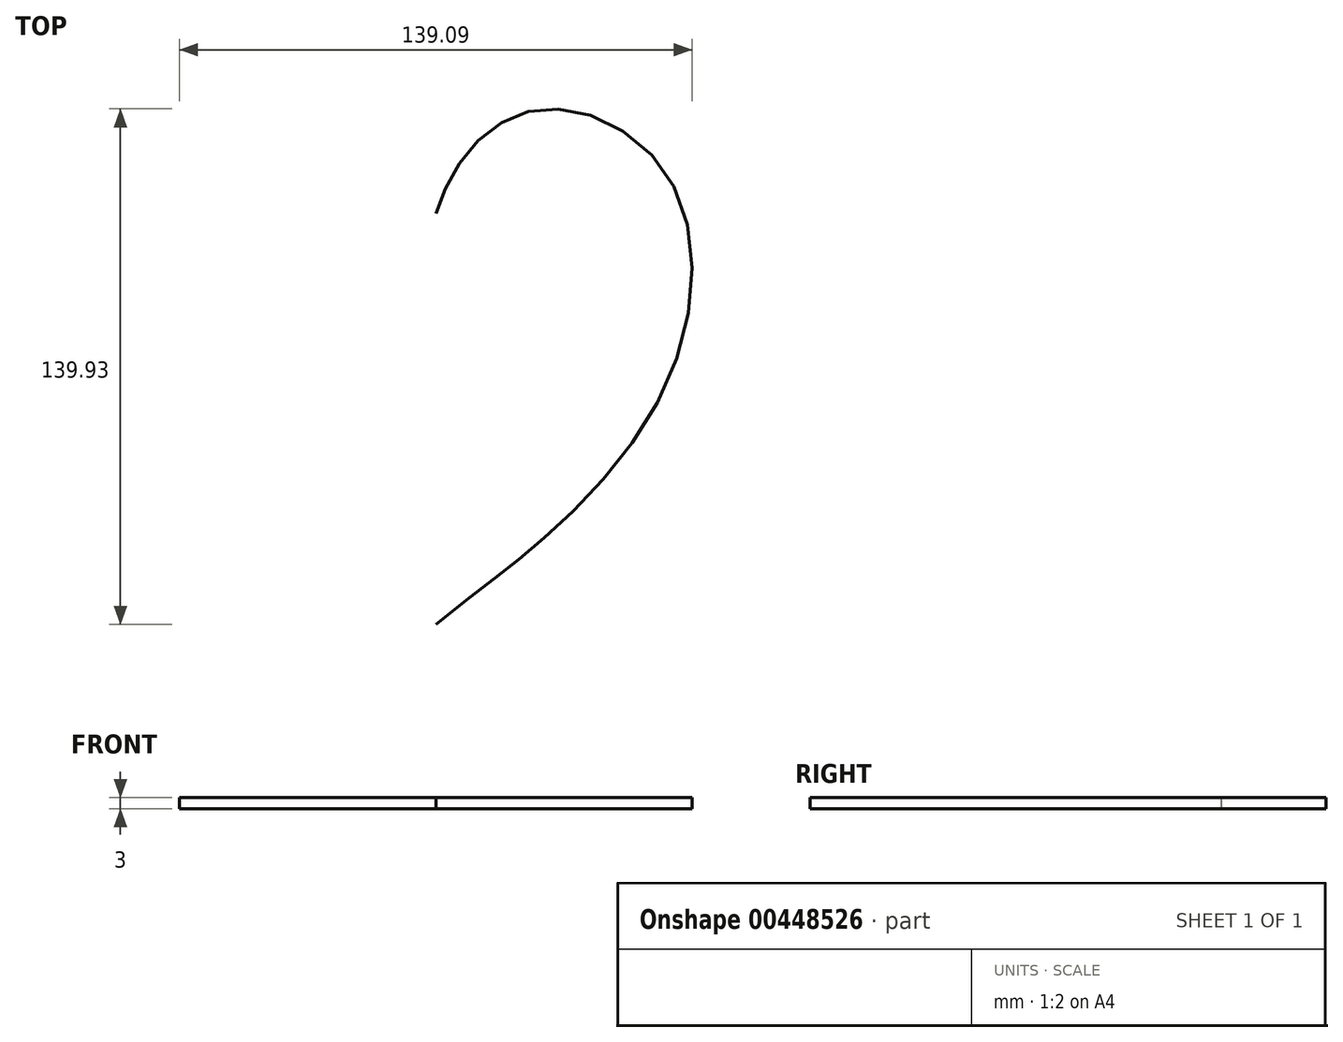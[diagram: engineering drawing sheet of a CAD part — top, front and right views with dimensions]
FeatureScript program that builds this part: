
annotation { "Feature Type Name" : "Feature", "Feature Type Description" : "" }
export const myFeature = defineFeature(function(context is Context, id is Id, definition is map)
    precondition{}
    {
        {
            var Q0;
            Q0=qCreatedBy(makeId("Top.planeOp"),FACE);
            var sketch = newSketch(context, id + "F0", { "sketchPlane" : qUnion([Q0])});
            skLineSegment(sketch, "E0", {"start": v(2.56, 36.8) * mm, "end": v(-183.57, 36.8) * mm, "construction": true});
            skLineSegment(sketch, "E1", {"start": v(2.56, 36.8) * mm, "end": v(157.98, 36.8) * mm, "construction": true});
            skFitSpline(sketch, "E2", {"points": [v(2.63, 8.53) * mm, v(-9.07, 28.5) * mm, v(-31.63, 36.8) * mm, v(-61.5, 16.74) * mm, v(-60.14, -37.44) * mm, v(-24.9, -81.19) * mm, v(2.63, -103) * mm], "startDerivative": vector(-43.82, 145.7) * mm, "endDerivative": vector(235.36, -190.2) * mm});
            skLineSegment(sketch, "E3", {"start": v(2.63, -103) * mm, "end": v(2.63, 28.57) * mm, "construction": true});
            skFitSpline(sketch, "E4.MirrorCS", {"points": [v(2.63, 8.53) * mm, v(14.32, 28.5) * mm, v(36.89, 36.8) * mm, v(66.75, 16.74) * mm, v(65.4, -37.44) * mm, v(30.15, -81.19) * mm, v(2.63, -103) * mm], "startDerivative": vector(43.82, 145.7) * mm, "endDerivative": vector(-235.36, -190.2) * mm});
            skSolve(sketch);
        }
        {
            var Q0;
            Q0=qSketchRegion(id+"F0",true);
            extrude(context, id + "F1", {"entities" : qUnion([Q0]), "depth" : 3 * mm});
        }
    });
